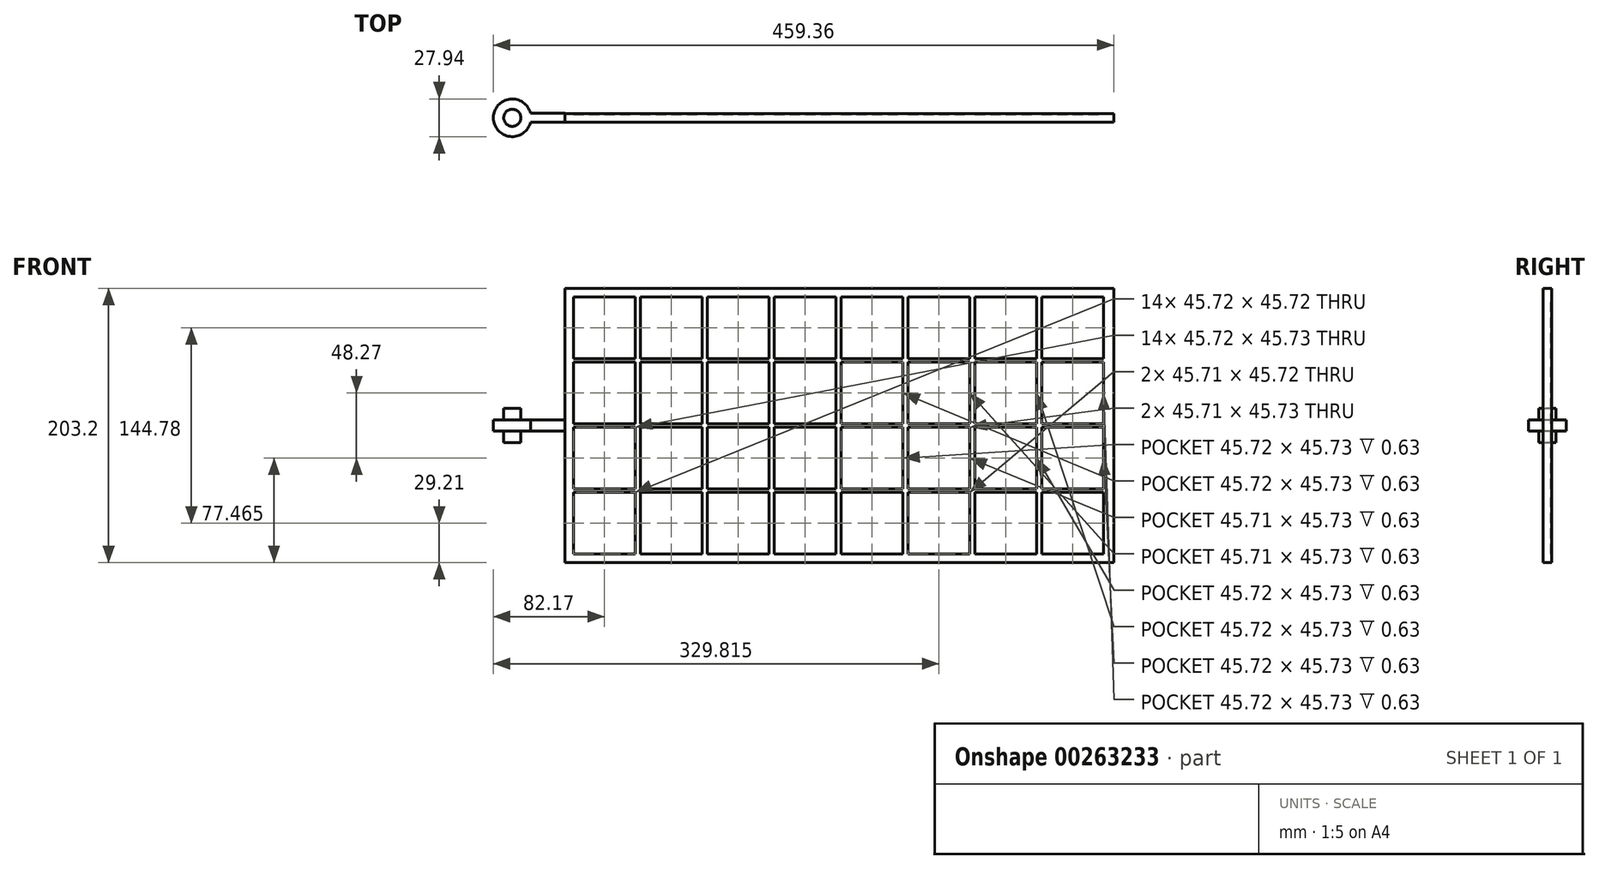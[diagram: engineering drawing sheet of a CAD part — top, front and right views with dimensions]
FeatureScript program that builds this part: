
annotation { "Feature Type Name" : "Feature", "Feature Type Description" : "" }
export const myFeature = defineFeature(function(context is Context, id is Id, definition is map)
    precondition{}
    {
        {
            var Q0;
            Q0=qCreatedBy(makeId("Top.planeOp"),FACE);
            var sketch = newSketch(context, id + "F0", { "sketchPlane" : qUnion([Q0])});
            skCircle(sketch, "E0", {"center": v(0, 0) * mm, "radius": 6.35 * mm});
            skSolve(sketch);
        }
        {
            var Q0;
            Q0=qSketchRegion(id+"F0",true);
            extrude(context, id + "F1", {"entities" : qUnion([Q0]), "endBound" : BoundingType.SYMMETRIC, "depth" : 25.4 * mm});
        }
        {
            var Q0;
            Q0=qCreatedBy(makeId("Top.planeOp"),FACE);
            var sketch = newSketch(context, id + "F2", { "sketchPlane" : qUnion([Q0])});
            skArc(sketch, "E1", {"start": v(13.59, 3.26) * mm, "mid": v(-13.97, 0) * mm, "end": v(13.59, -3.26) * mm});
            skCircle(sketch, "E2.0", {"center": v(0, 0) * mm, "radius": 6.35 * mm});
            skLineSegment(sketch, "E3", {"start": v(13.59, 3.26) * mm, "end": v(38.99, 3.26) * mm});
            skLineSegment(sketch, "E4", {"start": v(0, 0) * mm, "end": v(2.18, 0) * mm});
            skLineSegment(sketch, "E5.MirrorCS", {"start": v(13.59, -3.26) * mm, "end": v(38.99, -3.26) * mm});
            skLineSegment(sketch, "E6", {"start": v(38.99, 3.26) * mm, "end": v(38.99, -3.26) * mm});
            skSolve(sketch);
        }
        {
            var Q0;
            Q0=qSketchRegion(id+"F2",true);
            extrude(context, id + "F3", {"entities" : qUnion([Q0]), "operationType" : NewBodyOperationType.ADD, "endBound" : BoundingType.SYMMETRIC, "depth" : 8.38 * mm});
        }
        {
            var Q0;
            Q0=qCreatedBy(makeId("Front.planeOp"),FACE);
            var sketch = newSketch(context, id + "F4", { "sketchPlane" : qUnion([Q0])});
            skLineSegment(sketch, "E7.0", {"start": v(38.99, 4.2) * mm, "end": v(38.99, -4.2) * mm});
            skLineSegment(sketch, "E8", {"start": v(38.99, 0) * mm, "end": v(38.99, 101.6) * mm});
            skPoint(sketch, "E8.endSnap0", {"position": v(38.99, 0) * mm});
            skLineSegment(sketch, "E9", {"start": v(38.99, 0) * mm, "end": v(38.99, -101.6) * mm});
            skLineSegment(sketch, "E10", {"start": v(38.99, 101.6) * mm, "end": v(445.39, 101.6) * mm});
            skLineSegment(sketch, "E11.top", {"start": v(38.99, -101.6) * mm, "end": v(445.39, -101.6) * mm});
            skLineSegment(sketch, "E11.left", {"start": v(38.99, 101.6) * mm, "end": v(38.99, -101.6) * mm});
            skLineSegment(sketch, "E11.right", {"start": v(445.39, 101.6) * mm, "end": v(445.39, -101.6) * mm});
            skLineSegment(sketch, "E12.bottom", {"start": v(45.34, -95.25) * mm, "end": v(91.06, -95.25) * mm});
            skLineSegment(sketch, "E12.top", {"start": v(45.34, -49.53) * mm, "end": v(91.06, -49.53) * mm});
            skLineSegment(sketch, "E12.left", {"start": v(45.34, -95.25) * mm, "end": v(45.34, -49.53) * mm});
            skLineSegment(sketch, "E12.right", {"start": v(91.06, -95.25) * mm, "end": v(91.06, -49.53) * mm});
            skLineSegment(sketch, "E13.0.1.0", {"start": v(91.06, -47) * mm, "end": v(91.06, -1.27) * mm});
            skLineSegment(sketch, "E13.0.1.1", {"start": v(45.34, -47) * mm, "end": v(45.34, -1.27) * mm});
            skLineSegment(sketch, "E13.0.1.2", {"start": v(45.34, -1.27) * mm, "end": v(91.06, -1.27) * mm});
            skLineSegment(sketch, "E13.0.1.3", {"start": v(45.34, -47) * mm, "end": v(91.06, -47) * mm});
            skLineSegment(sketch, "E13.0.2.0", {"start": v(91.06, 1.27) * mm, "end": v(91.06, 47) * mm});
            skLineSegment(sketch, "E13.0.2.1", {"start": v(45.34, 1.27) * mm, "end": v(45.34, 47) * mm});
            skLineSegment(sketch, "E13.0.2.2", {"start": v(45.34, 47) * mm, "end": v(91.06, 47) * mm});
            skLineSegment(sketch, "E13.0.2.3", {"start": v(45.34, 1.27) * mm, "end": v(91.06, 1.27) * mm});
            skLineSegment(sketch, "E13.0.3.0", {"start": v(91.06, 49.53) * mm, "end": v(91.06, 95.25) * mm});
            skLineSegment(sketch, "E13.0.3.1", {"start": v(45.34, 49.53) * mm, "end": v(45.34, 95.25) * mm});
            skLineSegment(sketch, "E13.0.3.2", {"start": v(45.34, 95.25) * mm, "end": v(91.06, 95.25) * mm});
            skLineSegment(sketch, "E13.0.3.3", {"start": v(45.34, 49.53) * mm, "end": v(91.06, 49.53) * mm});
            skLineSegment(sketch, "E13.1.0.0", {"start": v(140.59, -95.25) * mm, "end": v(140.59, -49.53) * mm});
            skLineSegment(sketch, "E13.1.0.1", {"start": v(94.87, -95.25) * mm, "end": v(94.87, -49.53) * mm});
            skLineSegment(sketch, "E13.1.0.2", {"start": v(94.87, -49.53) * mm, "end": v(140.59, -49.53) * mm});
            skLineSegment(sketch, "E13.1.0.3", {"start": v(94.87, -95.25) * mm, "end": v(140.59, -95.25) * mm});
            skLineSegment(sketch, "E13.1.1.0", {"start": v(140.59, -47) * mm, "end": v(140.59, -1.27) * mm});
            skLineSegment(sketch, "E13.1.1.1", {"start": v(94.87, -47) * mm, "end": v(94.87, -1.27) * mm});
            skLineSegment(sketch, "E13.1.1.2", {"start": v(94.87, -1.27) * mm, "end": v(140.59, -1.27) * mm});
            skLineSegment(sketch, "E13.1.1.3", {"start": v(94.87, -47) * mm, "end": v(140.59, -47) * mm});
            skLineSegment(sketch, "E13.1.2.0", {"start": v(140.59, 1.27) * mm, "end": v(140.59, 47) * mm});
            skLineSegment(sketch, "E13.1.2.1", {"start": v(94.87, 1.27) * mm, "end": v(94.87, 47) * mm});
            skLineSegment(sketch, "E13.1.2.2", {"start": v(94.87, 47) * mm, "end": v(140.59, 47) * mm});
            skLineSegment(sketch, "E13.1.2.3", {"start": v(94.87, 1.27) * mm, "end": v(140.59, 1.27) * mm});
            skLineSegment(sketch, "E13.1.3.0", {"start": v(140.59, 49.53) * mm, "end": v(140.59, 95.25) * mm});
            skLineSegment(sketch, "E13.1.3.1", {"start": v(94.87, 49.53) * mm, "end": v(94.87, 95.25) * mm});
            skLineSegment(sketch, "E13.1.3.2", {"start": v(94.87, 95.25) * mm, "end": v(140.59, 95.25) * mm});
            skLineSegment(sketch, "E13.1.3.3", {"start": v(94.87, 49.53) * mm, "end": v(140.59, 49.53) * mm});
            skLineSegment(sketch, "E13.2.0.0", {"start": v(190.12, -95.25) * mm, "end": v(190.12, -49.53) * mm});
            skLineSegment(sketch, "E13.2.0.1", {"start": v(144.4, -95.25) * mm, "end": v(144.4, -49.53) * mm});
            skLineSegment(sketch, "E13.2.0.2", {"start": v(144.4, -49.53) * mm, "end": v(190.12, -49.53) * mm});
            skLineSegment(sketch, "E13.2.0.3", {"start": v(144.4, -95.25) * mm, "end": v(190.12, -95.25) * mm});
            skLineSegment(sketch, "E13.2.1.0", {"start": v(190.12, -47) * mm, "end": v(190.12, -1.27) * mm});
            skLineSegment(sketch, "E13.2.1.1", {"start": v(144.4, -47) * mm, "end": v(144.4, -1.27) * mm});
            skLineSegment(sketch, "E13.2.1.2", {"start": v(144.4, -1.27) * mm, "end": v(190.12, -1.27) * mm});
            skLineSegment(sketch, "E13.2.1.3", {"start": v(144.4, -47) * mm, "end": v(190.12, -47) * mm});
            skLineSegment(sketch, "E13.2.2.0", {"start": v(190.12, 1.27) * mm, "end": v(190.12, 47) * mm});
            skLineSegment(sketch, "E13.2.2.1", {"start": v(144.4, 1.27) * mm, "end": v(144.4, 47) * mm});
            skLineSegment(sketch, "E13.2.2.2", {"start": v(144.4, 47) * mm, "end": v(190.12, 47) * mm});
            skLineSegment(sketch, "E13.2.2.3", {"start": v(144.4, 1.27) * mm, "end": v(190.12, 1.27) * mm});
            skLineSegment(sketch, "E13.2.3.0", {"start": v(190.12, 49.53) * mm, "end": v(190.12, 95.25) * mm});
            skLineSegment(sketch, "E13.2.3.1", {"start": v(144.4, 49.53) * mm, "end": v(144.4, 95.25) * mm});
            skLineSegment(sketch, "E13.2.3.2", {"start": v(144.4, 95.25) * mm, "end": v(190.12, 95.25) * mm});
            skLineSegment(sketch, "E13.2.3.3", {"start": v(144.4, 49.53) * mm, "end": v(190.12, 49.53) * mm});
            skLineSegment(sketch, "E13.3.0.0", {"start": v(239.65, -95.25) * mm, "end": v(239.65, -49.53) * mm});
            skLineSegment(sketch, "E13.3.0.1", {"start": v(193.93, -95.25) * mm, "end": v(193.93, -49.53) * mm});
            skLineSegment(sketch, "E13.3.0.2", {"start": v(193.93, -49.53) * mm, "end": v(239.65, -49.53) * mm});
            skLineSegment(sketch, "E13.3.0.3", {"start": v(193.93, -95.25) * mm, "end": v(239.65, -95.25) * mm});
            skLineSegment(sketch, "E13.3.1.0", {"start": v(239.65, -47) * mm, "end": v(239.65, -1.27) * mm});
            skLineSegment(sketch, "E13.3.1.1", {"start": v(193.93, -47) * mm, "end": v(193.93, -1.27) * mm});
            skLineSegment(sketch, "E13.3.1.2", {"start": v(193.93, -1.27) * mm, "end": v(239.65, -1.27) * mm});
            skLineSegment(sketch, "E13.3.1.3", {"start": v(193.93, -47) * mm, "end": v(239.65, -47) * mm});
            skLineSegment(sketch, "E13.3.2.0", {"start": v(239.65, 1.27) * mm, "end": v(239.65, 47) * mm});
            skLineSegment(sketch, "E13.3.2.1", {"start": v(193.93, 1.27) * mm, "end": v(193.93, 47) * mm});
            skLineSegment(sketch, "E13.3.2.2", {"start": v(193.93, 47) * mm, "end": v(239.65, 47) * mm});
            skLineSegment(sketch, "E13.3.2.3", {"start": v(193.93, 1.27) * mm, "end": v(239.65, 1.27) * mm});
            skLineSegment(sketch, "E13.3.3.0", {"start": v(239.65, 49.53) * mm, "end": v(239.65, 95.25) * mm});
            skLineSegment(sketch, "E13.3.3.1", {"start": v(193.93, 49.53) * mm, "end": v(193.93, 95.25) * mm});
            skLineSegment(sketch, "E13.3.3.2", {"start": v(193.93, 95.25) * mm, "end": v(239.65, 95.25) * mm});
            skLineSegment(sketch, "E13.3.3.3", {"start": v(193.93, 49.53) * mm, "end": v(239.65, 49.53) * mm});
            skLineSegment(sketch, "E13.4.0.0", {"start": v(289.18, -95.25) * mm, "end": v(289.18, -49.53) * mm});
            skLineSegment(sketch, "E13.4.0.1", {"start": v(243.46, -95.25) * mm, "end": v(243.46, -49.53) * mm});
            skLineSegment(sketch, "E13.4.0.2", {"start": v(243.46, -49.53) * mm, "end": v(289.18, -49.53) * mm});
            skLineSegment(sketch, "E13.4.0.3", {"start": v(243.46, -95.25) * mm, "end": v(289.18, -95.25) * mm});
            skLineSegment(sketch, "E13.4.1.0", {"start": v(289.18, -47) * mm, "end": v(289.18, -1.27) * mm});
            skLineSegment(sketch, "E13.4.1.1", {"start": v(243.46, -47) * mm, "end": v(243.46, -1.27) * mm});
            skLineSegment(sketch, "E13.4.1.2", {"start": v(243.46, -1.27) * mm, "end": v(289.18, -1.27) * mm});
            skLineSegment(sketch, "E13.4.1.3", {"start": v(243.46, -47) * mm, "end": v(289.18, -47) * mm});
            skLineSegment(sketch, "E13.4.2.0", {"start": v(289.18, 1.27) * mm, "end": v(289.18, 47) * mm});
            skLineSegment(sketch, "E13.4.2.1", {"start": v(243.46, 1.27) * mm, "end": v(243.46, 47) * mm});
            skLineSegment(sketch, "E13.4.2.2", {"start": v(243.46, 47) * mm, "end": v(289.18, 47) * mm});
            skLineSegment(sketch, "E13.4.2.3", {"start": v(243.46, 1.27) * mm, "end": v(289.18, 1.27) * mm});
            skLineSegment(sketch, "E13.4.3.0", {"start": v(289.18, 49.53) * mm, "end": v(289.18, 95.25) * mm});
            skLineSegment(sketch, "E13.4.3.1", {"start": v(243.46, 49.53) * mm, "end": v(243.46, 95.25) * mm});
            skLineSegment(sketch, "E13.4.3.2", {"start": v(243.46, 95.25) * mm, "end": v(289.18, 95.25) * mm});
            skLineSegment(sketch, "E13.4.3.3", {"start": v(243.46, 49.53) * mm, "end": v(289.18, 49.53) * mm});
            skLineSegment(sketch, "E13.5.0.0", {"start": v(338.7, -95.25) * mm, "end": v(338.7, -49.53) * mm});
            skLineSegment(sketch, "E13.5.0.1", {"start": v(292.99, -95.25) * mm, "end": v(292.99, -49.53) * mm});
            skLineSegment(sketch, "E13.5.0.2", {"start": v(292.99, -49.53) * mm, "end": v(338.7, -49.53) * mm});
            skLineSegment(sketch, "E13.5.0.3", {"start": v(292.99, -95.25) * mm, "end": v(338.7, -95.25) * mm});
            skLineSegment(sketch, "E13.5.1.0", {"start": v(338.7, -47) * mm, "end": v(338.7, -1.27) * mm});
            skLineSegment(sketch, "E13.5.1.1", {"start": v(292.99, -47) * mm, "end": v(292.99, -1.27) * mm});
            skLineSegment(sketch, "E13.5.1.2", {"start": v(292.99, -1.27) * mm, "end": v(338.7, -1.27) * mm});
            skLineSegment(sketch, "E13.5.1.3", {"start": v(292.99, -47) * mm, "end": v(338.7, -47) * mm});
            skLineSegment(sketch, "E13.5.2.0", {"start": v(338.7, 1.27) * mm, "end": v(338.7, 47) * mm});
            skLineSegment(sketch, "E13.5.2.1", {"start": v(292.99, 1.27) * mm, "end": v(292.99, 47) * mm});
            skLineSegment(sketch, "E13.5.2.2", {"start": v(292.99, 47) * mm, "end": v(338.7, 47) * mm});
            skLineSegment(sketch, "E13.5.2.3", {"start": v(292.99, 1.27) * mm, "end": v(338.7, 1.27) * mm});
            skLineSegment(sketch, "E13.5.3.0", {"start": v(338.7, 49.53) * mm, "end": v(338.7, 95.25) * mm});
            skLineSegment(sketch, "E13.5.3.1", {"start": v(292.99, 49.53) * mm, "end": v(292.99, 95.25) * mm});
            skLineSegment(sketch, "E13.5.3.2", {"start": v(292.99, 95.25) * mm, "end": v(338.7, 95.25) * mm});
            skLineSegment(sketch, "E13.5.3.3", {"start": v(292.99, 49.53) * mm, "end": v(338.7, 49.53) * mm});
            skLineSegment(sketch, "E13.6.0.0", {"start": v(388.24, -95.25) * mm, "end": v(388.24, -49.53) * mm});
            skLineSegment(sketch, "E13.6.0.1", {"start": v(342.52, -95.25) * mm, "end": v(342.52, -49.53) * mm});
            skLineSegment(sketch, "E13.6.0.2", {"start": v(342.52, -49.53) * mm, "end": v(388.24, -49.53) * mm});
            skLineSegment(sketch, "E13.6.0.3", {"start": v(342.52, -95.25) * mm, "end": v(388.24, -95.25) * mm});
            skLineSegment(sketch, "E13.6.1.0", {"start": v(388.24, -47) * mm, "end": v(388.24, -1.27) * mm});
            skLineSegment(sketch, "E13.6.1.1", {"start": v(342.52, -47) * mm, "end": v(342.52, -1.27) * mm});
            skLineSegment(sketch, "E13.6.1.2", {"start": v(342.52, -1.27) * mm, "end": v(388.24, -1.27) * mm});
            skLineSegment(sketch, "E13.6.1.3", {"start": v(342.52, -47) * mm, "end": v(388.24, -47) * mm});
            skLineSegment(sketch, "E13.6.2.0", {"start": v(388.24, 1.27) * mm, "end": v(388.24, 47) * mm});
            skLineSegment(sketch, "E13.6.2.1", {"start": v(342.52, 1.27) * mm, "end": v(342.52, 47) * mm});
            skLineSegment(sketch, "E13.6.2.2", {"start": v(342.52, 47) * mm, "end": v(388.24, 47) * mm});
            skLineSegment(sketch, "E13.6.2.3", {"start": v(342.52, 1.27) * mm, "end": v(388.24, 1.27) * mm});
            skLineSegment(sketch, "E13.6.3.0", {"start": v(388.24, 49.53) * mm, "end": v(388.24, 95.25) * mm});
            skLineSegment(sketch, "E13.6.3.1", {"start": v(342.52, 49.53) * mm, "end": v(342.52, 95.25) * mm});
            skLineSegment(sketch, "E13.6.3.2", {"start": v(342.52, 95.25) * mm, "end": v(388.24, 95.25) * mm});
            skLineSegment(sketch, "E13.6.3.3", {"start": v(342.52, 49.53) * mm, "end": v(388.24, 49.53) * mm});
            skLineSegment(sketch, "E13.7.0.0", {"start": v(437.77, -95.25) * mm, "end": v(437.77, -49.53) * mm});
            skLineSegment(sketch, "E13.7.0.1", {"start": v(392.05, -95.25) * mm, "end": v(392.05, -49.53) * mm});
            skLineSegment(sketch, "E13.7.0.2", {"start": v(392.05, -49.53) * mm, "end": v(437.77, -49.53) * mm});
            skLineSegment(sketch, "E13.7.0.3", {"start": v(392.05, -95.25) * mm, "end": v(437.77, -95.25) * mm});
            skLineSegment(sketch, "E13.7.1.0", {"start": v(437.77, -47) * mm, "end": v(437.77, -1.27) * mm});
            skLineSegment(sketch, "E13.7.1.1", {"start": v(392.05, -47) * mm, "end": v(392.05, -1.27) * mm});
            skLineSegment(sketch, "E13.7.1.2", {"start": v(392.05, -1.27) * mm, "end": v(437.77, -1.27) * mm});
            skLineSegment(sketch, "E13.7.1.3", {"start": v(392.05, -47) * mm, "end": v(437.77, -47) * mm});
            skLineSegment(sketch, "E13.7.2.0", {"start": v(437.77, 1.27) * mm, "end": v(437.77, 47) * mm});
            skLineSegment(sketch, "E13.7.2.1", {"start": v(392.05, 1.27) * mm, "end": v(392.05, 47) * mm});
            skLineSegment(sketch, "E13.7.2.2", {"start": v(392.05, 47) * mm, "end": v(437.77, 47) * mm});
            skLineSegment(sketch, "E13.7.2.3", {"start": v(392.05, 1.27) * mm, "end": v(437.77, 1.27) * mm});
            skLineSegment(sketch, "E13.7.3.0", {"start": v(437.77, 49.53) * mm, "end": v(437.77, 95.25) * mm});
            skLineSegment(sketch, "E13.7.3.1", {"start": v(392.05, 49.53) * mm, "end": v(392.05, 95.25) * mm});
            skLineSegment(sketch, "E13.7.3.2", {"start": v(392.05, 95.25) * mm, "end": v(437.77, 95.25) * mm});
            skLineSegment(sketch, "E13.7.3.3", {"start": v(392.05, 49.53) * mm, "end": v(437.77, 49.53) * mm});
            skLineSegment(sketch, "E13.direction1", {"start": v(45.34, -95.25) * mm, "end": v(94.87, -95.25) * mm, "construction": true});
            skLineSegment(sketch, "E13.direction2", {"start": v(45.34, -95.25) * mm, "end": v(45.34, -47) * mm, "construction": true});
            skSolve(sketch);
        }
        {
            var Q0;
            Q0=qSketchRegion(id+"F4",true);
            extrude(context, id + "F5", {"entities" : qUnion([Q0]), "operationType" : NewBodyOperationType.ADD, "oppositeDirection" : true, "depth" : 3.17 * mm});
        }
        {
            var Q0;
            Q0=makeQuery(id+"F5.opExtrude","CAP_FACE",FACE,{"disambiguationData":[OSD([sQuery(id+"F4.wireOp",EDGE,"E10"),sQuery(id+"F4.wireOp",EDGE,"E11.top"),sQuery(id+"F4.wireOp",EDGE,"E11.left"),sQuery(id+"F4.wireOp",EDGE,"E11.right"),sQuery(id+"F4.wireOp",EDGE,"E12.bottom"),sQuery(id+"F4.wireOp",EDGE,"E12.top"),sQuery(id+"F4.wireOp",EDGE,"E12.left"),sQuery(id+"F4.wireOp",EDGE,"E12.right"),sQuery(id+"F4.wireOp",EDGE,"E13.0.1.0"),sQuery(id+"F4.wireOp",EDGE,"E13.0.1.1"),sQuery(id+"F4.wireOp",EDGE,"E13.0.1.2"),sQuery(id+"F4.wireOp",EDGE,"E13.0.1.3"),sQuery(id+"F4.wireOp",EDGE,"E13.0.2.0"),sQuery(id+"F4.wireOp",EDGE,"E13.0.2.1"),sQuery(id+"F4.wireOp",EDGE,"E13.0.2.2"),sQuery(id+"F4.wireOp",EDGE,"E13.0.2.3"),sQuery(id+"F4.wireOp",EDGE,"E13.0.3.0"),sQuery(id+"F4.wireOp",EDGE,"E13.0.3.1"),sQuery(id+"F4.wireOp",EDGE,"E13.0.3.2"),sQuery(id+"F4.wireOp",EDGE,"E13.0.3.3"),sQuery(id+"F4.wireOp",EDGE,"E13.1.0.0"),sQuery(id+"F4.wireOp",EDGE,"E13.1.0.1"),sQuery(id+"F4.wireOp",EDGE,"E13.1.0.2"),sQuery(id+"F4.wireOp",EDGE,"E13.1.0.3"),sQuery(id+"F4.wireOp",EDGE,"E13.1.1.0"),sQuery(id+"F4.wireOp",EDGE,"E13.1.1.1"),sQuery(id+"F4.wireOp",EDGE,"E13.1.1.2"),sQuery(id+"F4.wireOp",EDGE,"E13.1.1.3"),sQuery(id+"F4.wireOp",EDGE,"E13.1.2.0"),sQuery(id+"F4.wireOp",EDGE,"E13.1.2.1"),sQuery(id+"F4.wireOp",EDGE,"E13.1.2.2"),sQuery(id+"F4.wireOp",EDGE,"E13.1.2.3"),sQuery(id+"F4.wireOp",EDGE,"E13.1.3.0"),sQuery(id+"F4.wireOp",EDGE,"E13.1.3.1"),sQuery(id+"F4.wireOp",EDGE,"E13.1.3.2"),sQuery(id+"F4.wireOp",EDGE,"E13.1.3.3"),sQuery(id+"F4.wireOp",EDGE,"E13.2.0.0"),sQuery(id+"F4.wireOp",EDGE,"E13.2.0.1"),sQuery(id+"F4.wireOp",EDGE,"E13.2.0.2"),sQuery(id+"F4.wireOp",EDGE,"E13.2.0.3"),sQuery(id+"F4.wireOp",EDGE,"E13.2.1.0"),sQuery(id+"F4.wireOp",EDGE,"E13.2.1.1"),sQuery(id+"F4.wireOp",EDGE,"E13.2.1.2"),sQuery(id+"F4.wireOp",EDGE,"E13.2.1.3"),sQuery(id+"F4.wireOp",EDGE,"E13.2.2.0"),sQuery(id+"F4.wireOp",EDGE,"E13.2.2.1"),sQuery(id+"F4.wireOp",EDGE,"E13.2.2.2"),sQuery(id+"F4.wireOp",EDGE,"E13.2.2.3"),sQuery(id+"F4.wireOp",EDGE,"E13.2.3.0"),sQuery(id+"F4.wireOp",EDGE,"E13.2.3.1"),sQuery(id+"F4.wireOp",EDGE,"E13.2.3.2"),sQuery(id+"F4.wireOp",EDGE,"E13.2.3.3"),sQuery(id+"F4.wireOp",EDGE,"E13.3.0.0"),sQuery(id+"F4.wireOp",EDGE,"E13.3.0.1"),sQuery(id+"F4.wireOp",EDGE,"E13.3.0.2"),sQuery(id+"F4.wireOp",EDGE,"E13.3.0.3"),sQuery(id+"F4.wireOp",EDGE,"E13.3.1.0"),sQuery(id+"F4.wireOp",EDGE,"E13.3.1.1"),sQuery(id+"F4.wireOp",EDGE,"E13.3.1.2"),sQuery(id+"F4.wireOp",EDGE,"E13.3.1.3"),sQuery(id+"F4.wireOp",EDGE,"E13.3.2.0"),sQuery(id+"F4.wireOp",EDGE,"E13.3.2.1"),sQuery(id+"F4.wireOp",EDGE,"E13.3.2.2"),sQuery(id+"F4.wireOp",EDGE,"E13.3.2.3"),sQuery(id+"F4.wireOp",EDGE,"E13.3.3.0"),sQuery(id+"F4.wireOp",EDGE,"E13.3.3.1"),sQuery(id+"F4.wireOp",EDGE,"E13.3.3.2"),sQuery(id+"F4.wireOp",EDGE,"E13.3.3.3"),sQuery(id+"F4.wireOp",EDGE,"E13.4.0.0"),sQuery(id+"F4.wireOp",EDGE,"E13.4.0.1"),sQuery(id+"F4.wireOp",EDGE,"E13.4.0.2"),sQuery(id+"F4.wireOp",EDGE,"E13.4.0.3"),sQuery(id+"F4.wireOp",EDGE,"E13.4.1.0"),sQuery(id+"F4.wireOp",EDGE,"E13.4.1.1"),sQuery(id+"F4.wireOp",EDGE,"E13.4.1.2"),sQuery(id+"F4.wireOp",EDGE,"E13.4.1.3"),sQuery(id+"F4.wireOp",EDGE,"E13.4.2.0"),sQuery(id+"F4.wireOp",EDGE,"E13.4.2.1"),sQuery(id+"F4.wireOp",EDGE,"E13.4.2.2"),sQuery(id+"F4.wireOp",EDGE,"E13.4.2.3"),sQuery(id+"F4.wireOp",EDGE,"E13.4.3.0"),sQuery(id+"F4.wireOp",EDGE,"E13.4.3.1"),sQuery(id+"F4.wireOp",EDGE,"E13.4.3.2"),sQuery(id+"F4.wireOp",EDGE,"E13.4.3.3"),sQuery(id+"F4.wireOp",EDGE,"E13.5.0.0"),sQuery(id+"F4.wireOp",EDGE,"E13.5.0.1"),sQuery(id+"F4.wireOp",EDGE,"E13.5.0.2"),sQuery(id+"F4.wireOp",EDGE,"E13.5.0.3"),sQuery(id+"F4.wireOp",EDGE,"E13.5.1.0"),sQuery(id+"F4.wireOp",EDGE,"E13.5.1.1"),sQuery(id+"F4.wireOp",EDGE,"E13.5.1.2"),sQuery(id+"F4.wireOp",EDGE,"E13.5.1.3"),sQuery(id+"F4.wireOp",EDGE,"E13.5.2.0"),sQuery(id+"F4.wireOp",EDGE,"E13.5.2.1"),sQuery(id+"F4.wireOp",EDGE,"E13.5.2.2"),sQuery(id+"F4.wireOp",EDGE,"E13.5.2.3"),sQuery(id+"F4.wireOp",EDGE,"E13.5.3.0"),sQuery(id+"F4.wireOp",EDGE,"E13.5.3.1"),sQuery(id+"F4.wireOp",EDGE,"E13.5.3.2"),sQuery(id+"F4.wireOp",EDGE,"E13.5.3.3"),sQuery(id+"F4.wireOp",EDGE,"E13.6.0.0"),sQuery(id+"F4.wireOp",EDGE,"E13.6.0.1"),sQuery(id+"F4.wireOp",EDGE,"E13.6.0.2"),sQuery(id+"F4.wireOp",EDGE,"E13.6.0.3"),sQuery(id+"F4.wireOp",EDGE,"E13.6.1.0"),sQuery(id+"F4.wireOp",EDGE,"E13.6.1.1"),sQuery(id+"F4.wireOp",EDGE,"E13.6.1.2"),sQuery(id+"F4.wireOp",EDGE,"E13.6.1.3"),sQuery(id+"F4.wireOp",EDGE,"E13.6.2.0"),sQuery(id+"F4.wireOp",EDGE,"E13.6.2.1"),sQuery(id+"F4.wireOp",EDGE,"E13.6.2.2"),sQuery(id+"F4.wireOp",EDGE,"E13.6.2.3"),sQuery(id+"F4.wireOp",EDGE,"E13.6.3.0"),sQuery(id+"F4.wireOp",EDGE,"E13.6.3.1"),sQuery(id+"F4.wireOp",EDGE,"E13.6.3.2"),sQuery(id+"F4.wireOp",EDGE,"E13.6.3.3"),sQuery(id+"F4.wireOp",EDGE,"E13.7.0.0"),sQuery(id+"F4.wireOp",EDGE,"E13.7.0.1"),sQuery(id+"F4.wireOp",EDGE,"E13.7.0.2"),sQuery(id+"F4.wireOp",EDGE,"E13.7.0.3"),sQuery(id+"F4.wireOp",EDGE,"E13.7.1.0"),sQuery(id+"F4.wireOp",EDGE,"E13.7.1.1"),sQuery(id+"F4.wireOp",EDGE,"E13.7.1.2"),sQuery(id+"F4.wireOp",EDGE,"E13.7.1.3"),sQuery(id+"F4.wireOp",EDGE,"E13.7.2.0"),sQuery(id+"F4.wireOp",EDGE,"E13.7.2.1"),sQuery(id+"F4.wireOp",EDGE,"E13.7.2.2"),sQuery(id+"F4.wireOp",EDGE,"E13.7.2.3"),sQuery(id+"F4.wireOp",EDGE,"E13.7.3.0"),sQuery(id+"F4.wireOp",EDGE,"E13.7.3.1"),sQuery(id+"F4.wireOp",EDGE,"E13.7.3.2"),sQuery(id+"F4.wireOp",EDGE,"E13.7.3.3")])],"isStart":true});
            var sketch = newSketch(context, id + "F6", { "sketchPlane" : qUnion([Q0])});
            skSolve(sketch);
        }
        {
            var Q0;
            {var subQ72=sQuery(id+"F4.wireOp",EDGE,"E10");Q0=makeQuery(id+"F6.imprint","IMPRINT",FACE,{"disambiguationData":[TD([[makeQuery(id+"F6.imprint","IMPRINT",EDGE,{"derivedFrom":makeQuery(id+"F5.opExtrude","CAP_EDGE",EDGE,{"disambiguationData":[OSD([subQ72])],"isStart":true})}),-1.0]])]});}
            var sketch = newSketch(context, id + "F7", { "sketchPlane" : qUnion([Q0])});
            skLineSegment(sketch, "E14.bottom", {"start": v(41.78, 98.8) * mm, "end": v(441.83, 98.8) * mm});
            skLineSegment(sketch, "E14.top", {"start": v(41.78, -98.04) * mm, "end": v(441.83, -98.04) * mm});
            skLineSegment(sketch, "E14.left", {"start": v(41.78, 98.8) * mm, "end": v(41.78, -98.04) * mm});
            skLineSegment(sketch, "E14.right", {"start": v(441.83, 98.8) * mm, "end": v(441.83, -98.04) * mm});
            skLineSegment(sketch, "E15.0", {"start": v(45.34, 49.53) * mm, "end": v(45.34, 95.25) * mm});
            skLineSegment(sketch, "E15.1", {"start": v(45.34, 95.25) * mm, "end": v(91.06, 95.25) * mm});
            skLineSegment(sketch, "E16.0", {"start": v(437.77, -95.25) * mm, "end": v(437.77, -49.53) * mm});
            skLineSegment(sketch, "E16.1", {"start": v(392.05, -95.25) * mm, "end": v(437.77, -95.25) * mm});
            skSolve(sketch);
        }
        {
            var Q0;
            Q0=qSketchRegion(id+"F7",true);
            extrude(context, id + "F8", {"entities" : qUnion([Q0]), "operationType" : NewBodyOperationType.REMOVE, "depth" : 190 * mm});
        }
        {
            var Q0;
            Q0=makeQuery(id+"F6.imprint","IMPRINT",FACE,{"disambiguationData":[TD([[makeQuery(id+"F6.imprint","IMPRINT",EDGE,{"derivedFrom":makeQuery(id+"F5.opExtrude","CAP_EDGE",EDGE,{"disambiguationData":[OSD([sQuery(id+"F4.wireOp",EDGE,"E13.2.3.0")])],"isStart":true})}),1.0]])]});
            cPlane(context, id + "F9", {"entities" : qUnion([Q0]), "cplaneType" : CPlaneType.OFFSET, "offset" : 2.54 * mm, "oppositeDirection" : true, "width" : 152.4 * mm, "height" : 152.4 * mm});
        }
        {
            var Q0;
            Q0=qCreatedBy(id+"F9.planeOp",FACE);
            var sketch = newSketch(context, id + "F10", { "sketchPlane" : qUnion([Q0])});
            skLineSegment(sketch, "E17.0", {"start": v(41.78, 98.8) * mm, "end": v(41.78, -98.04) * mm});
            skLineSegment(sketch, "E18.0", {"start": v(41.78, 98.8) * mm, "end": v(441.83, 98.8) * mm});
            skLineSegment(sketch, "E19.0", {"start": v(441.83, 98.8) * mm, "end": v(441.83, -98.04) * mm});
            skLineSegment(sketch, "E20.0", {"start": v(41.78, -98.04) * mm, "end": v(441.83, -98.04) * mm});
            skSolve(sketch);
        }
        {
            var Q0;
            Q0=qSketchRegion(id+"F10",true);
            extrude(context, id + "F11", {"entities" : qUnion([Q0]), "depth" : 5.08 * mm});
        }
        {
            var Q0;
            Q0=makeQuery(id+"F1.opExtrude","SWEPT_BODY",BODY,{"disambiguationData":[OSD([sQuery(id+"F0.wireOp",EDGE,"E0")])]});
            var Q1;
            {var subQ72=sQuery(id+"F4.wireOp",EDGE,"E10");Q1=makeQuery(id+"F6.imprint","IMPRINT",FACE,{"disambiguationData":[TD([[makeQuery(id+"F6.imprint","IMPRINT",EDGE,{"derivedFrom":makeQuery(id+"F5.opExtrude","CAP_EDGE",EDGE,{"disambiguationData":[OSD([subQ72])],"isStart":true})}),-1.0]])]});}
            mirror(context, id + "F12", {"operationType" : NewBodyOperationType.ADD, "entities" : qUnion([Q0]), "mirrorPlane" : qUnion([Q1])});
        }
    });
